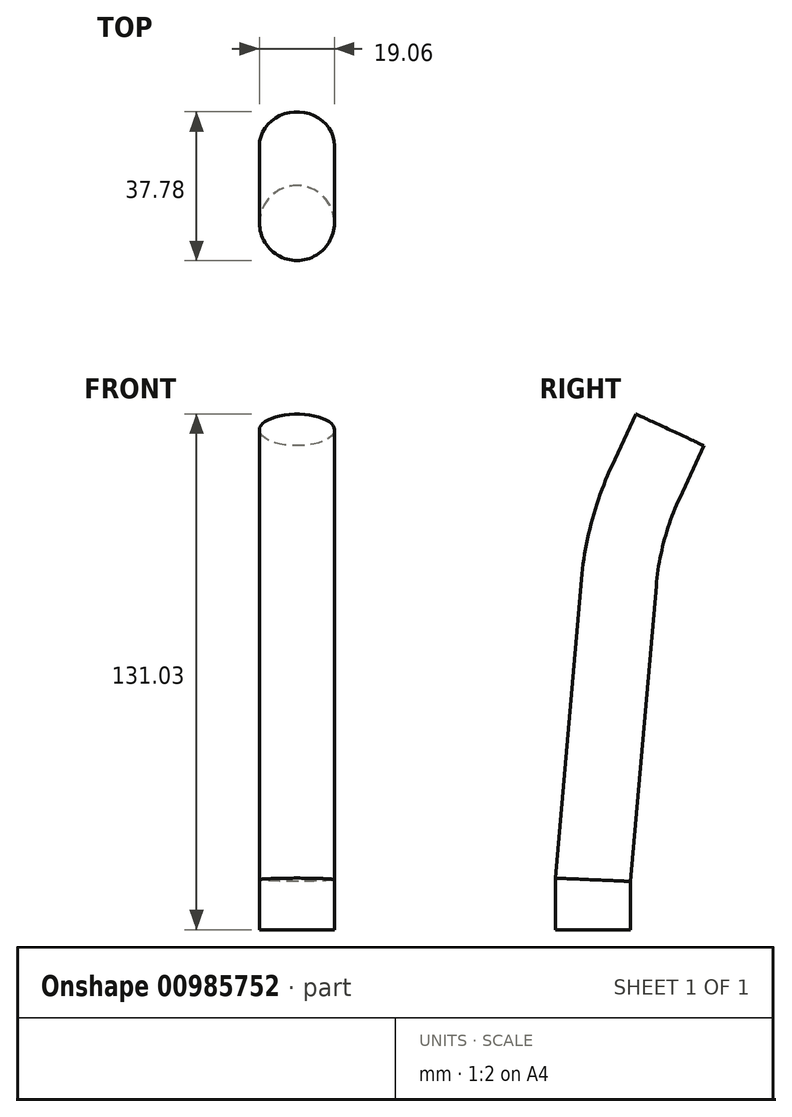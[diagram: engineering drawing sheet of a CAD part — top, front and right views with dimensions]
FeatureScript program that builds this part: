
annotation { "Feature Type Name" : "Feature", "Feature Type Description" : "" }
export const myFeature = defineFeature(function(context is Context, id is Id, definition is map)
    precondition{}
    {
        {
            var Q0;
            Q0=qCreatedBy(makeId("Right.planeOp"),FACE);
            var sketch = newSketch(context, id + "F0", { "sketchPlane" : qUnion([Q0])});
            skLineSegment(sketch, "E0", {"start": v(13.46, 113.78) * mm, "end": v(19.62, 127) * mm});
            skLineSegment(sketch, "E1", {"start": v(7.78, 101.6) * mm, "end": v(58.71, 101.6) * mm, "construction": true});
            skLineSegment(sketch, "E2", {"start": v(0, 0) * mm, "end": v(0, 121.8) * mm, "construction": true});
            skLineSegment(sketch, "E3", {"start": v(0, 0) * mm, "end": v(0, 12.7) * mm});
            skLineSegment(sketch, "E4", {"start": v(0, 12.7) * mm, "end": v(6.6, 88.22) * mm});
            skPoint(sketch, "E5.visualSharp", {"position": v(7.78, 101.6) * mm});
            skArc(sketch, "E5.filletArc", {"start": v(13.46, 113.78) * mm, "mid": v(8.91, 101.3) * mm, "end": v(6.6, 88.22) * mm});
            skSolve(sketch);
        }
        {
            var Q0;
            Q0=qCreatedBy(makeId("Top.planeOp"),FACE);
            var sketch = newSketch(context, id + "F1", { "sketchPlane" : qUnion([Q0])});
            skCircle(sketch, "E6", {"center": v(0, 0) * mm, "radius": 9.53 * mm});
            skSolve(sketch);
        }
        {
            var Q0;
            Q0=makeQuery(id+"F1.imprint","IMPRINT",FACE,{"disambiguationData":[TD([[makeQuery(id+"F1.imprint","IMPRINT",EDGE,{"derivedFrom":sQuery(id+"F1.wireOp",EDGE,"E6")}),1.0]])]});
            var Q1;
            Q1 = qConstructionFilter(qBodyType(qCreatedBy(id + "F0" ,EDGE), BodyType.WIRE), ConstructionObject.NO);
            sweep(context, id + "F2", {"profiles" : qUnion([Q0]), "path" : qUnion([Q1])});
        }
    });
